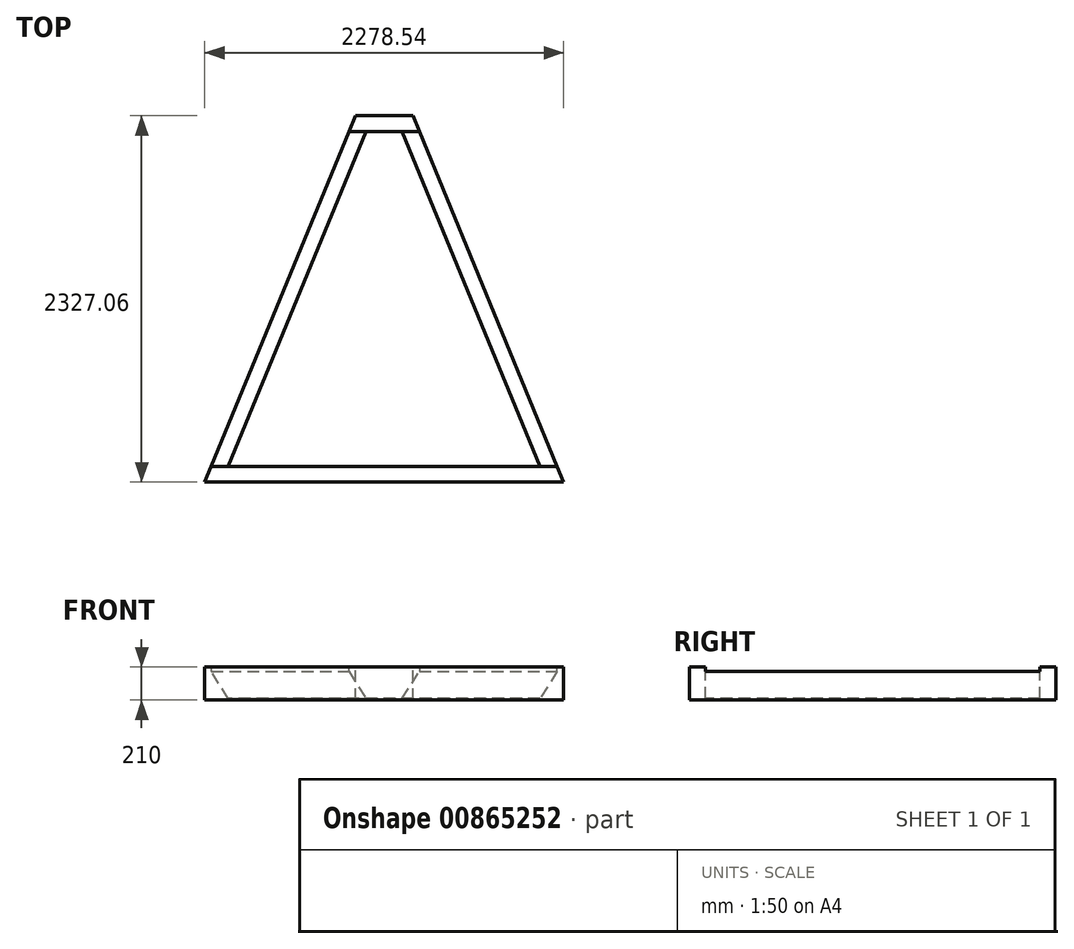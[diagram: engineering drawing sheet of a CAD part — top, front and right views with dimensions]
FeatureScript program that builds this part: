
annotation { "Feature Type Name" : "Feature", "Feature Type Description" : "" }
export const myFeature = defineFeature(function(context is Context, id is Id, definition is map)
    precondition{}
    {
        {
            var Q0;
            Q0=qCreatedBy(makeId("Top.planeOp"),FACE);
            var sketch = newSketch(context, id + "F0", { "sketchPlane" : qUnion([Q0])});
            skLineSegment(sketch, "E0", {"start": v(0, 0) * mm, "end": v(875, 2127.06) * mm});
            skLineSegment(sketch, "E1", {"start": v(875, 2127.06) * mm, "end": v(1105, 2127.06) * mm});
            skLineSegment(sketch, "E2", {"start": v(1105, 2127.06) * mm, "end": v(1980, 0) * mm});
            skLineSegment(sketch, "E3", {"start": v(1980, 0) * mm, "end": v(0, 0) * mm});
            skLineSegment(sketch, "E4.0", {"start": v(-149.27, -100) * mm, "end": v(808, 2227.06) * mm});
            skLineSegment(sketch, "E4.1", {"start": v(2129.27, -100) * mm, "end": v(-149.27, -100) * mm});
            skLineSegment(sketch, "E4.2", {"start": v(1172, 2227.06) * mm, "end": v(2129.27, -100) * mm});
            skLineSegment(sketch, "E4.3", {"start": v(808, 2227.06) * mm, "end": v(1172, 2227.06) * mm});
            skSolve(sketch);
        }
        {
            var Q0;
            Q0=makeQuery(id+"F0.imprint","IMPRINT",FACE,{"disambiguationData":[TD([[makeQuery(id+"F0.imprint","IMPRINT",EDGE,{"derivedFrom":sQuery(id+"F0.wireOp",EDGE,"E0")}),-1.0]])]});
            var Q1;
            Q1=makeQuery(id+"F0.imprint","IMPRINT",FACE,{"disambiguationData":[TD([[makeQuery(id+"F0.imprint","IMPRINT",EDGE,{"derivedFrom":sQuery(id+"F0.wireOp",EDGE,"E0")}),1.0]])]});
            extrude(context, id + "F1", {"entities" : qUnion([Q0, Q1]), "oppositeDirection" : true, "depth" : 10 * mm, "offsetDistance" : 25 * mm});
        }
        {
            var Q0;
            Q0=makeQuery(id+"F1.opExtrude","CAP_FACE",FACE,{"disambiguationData":[OSD([sQuery(id+"F0.wireOp",EDGE,"E4.0"),sQuery(id+"F0.wireOp",EDGE,"E4.1"),sQuery(id+"F0.wireOp",EDGE,"E4.2"),sQuery(id+"F0.wireOp",EDGE,"E4.3")])],"isStart":true});
            var sketch = newSketch(context, id + "F2", { "sketchPlane" : qUnion([Q0])});
            skLineSegment(sketch, "E5.0", {"start": v(0, 0) * mm, "end": v(875, 2127.06) * mm});
            skLineSegment(sketch, "E5.1", {"start": v(1980, 0) * mm, "end": v(0, 0) * mm});
            skLineSegment(sketch, "E5.2", {"start": v(1105, 2127.06) * mm, "end": v(1980, 0) * mm});
            skLineSegment(sketch, "E5.3", {"start": v(875, 2127.06) * mm, "end": v(1105, 2127.06) * mm});
            skSolve(sketch);
        }
        {
            var Q0;
            Q0=makeQuery(id+"F2.imprint","IMPRINT",FACE,{"disambiguationData":[TD([[makeQuery(id+"F2.imprint","IMPRINT",EDGE,{"derivedFrom":sQuery(id+"F2.wireOp",EDGE,"E5.0")}),1.0]])]});
            extrude(context, id + "F3", {"entities" : qUnion([Q0]), "operationType" : NewBodyOperationType.ADD, "depth" : 200 * mm, "offsetDistance" : 25 * mm});
        }
        {
            var Q0;
            Q0=makeQuery(id+"F3.opExtrude","CAP_EDGE",EDGE,{"disambiguationData":[OSD([sQuery(id+"F2.wireOp",EDGE,"E5.0")])],"isStart":false});
            var Q1;
            Q1=makeQuery(id+"F3.opExtrude","CAP_EDGE",EDGE,{"disambiguationData":[OSD([sQuery(id+"F2.wireOp",EDGE,"E5.2")])],"isStart":false});
            chamfer(context, id + "F4", {"entities" : qUnion([Q0, Q1]), "chamferType" : ChamferType.OFFSET_ANGLE, "width" : 200 * mm, "oppositeDirection" : true, "angle" : 30 * degree, "tangentPropagation" : true});
        }
    });
